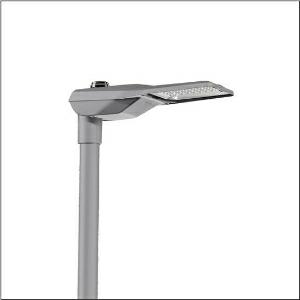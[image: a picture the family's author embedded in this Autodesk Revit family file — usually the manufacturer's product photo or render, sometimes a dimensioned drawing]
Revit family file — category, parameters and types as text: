
# Revit family: streetlight_sl_21_mini___p0_8a_5xe6u27n08hb_f017
name_source: partatom
category: Lighting Fixtures
units: mm (PartAtom-declared; Revit-internal decimal feet)

## family parameters
Cut with Voids When Loaded = No
Host = Face
Light Source = No
Part Type = Normal
Room Calculation Point = No
Round Connector Dimension = Use Diameter
Shared = No

## types (1)
- --- (1 x LED, 7550 lm, 66 W, 2200K)
    Apparent Load = 66 VA
    CIE Flux Codes = 33 69 96 100 100
    Color Rendering = 70
    Color Temperature = 2200K
    Default Elevation = 1800 mm
    Description = Streetlight SL 21 mini, mast luminaire, primary light control with lens, of PMMA, primary optical cover: cover, of toughened safety glass, transparent, light distribution: P0.8a, light emission: direct distribution, primary light characteristic: asymmetric, installation type: side-entry, LED, 3G 1.5mm², High Power LED, rated luminous flux: 7.550lm, luminous efficacy: 114lm/W, light colour: 722, colour temperature: 2200K, control gear: NEMA (7pin), control: flexible luminous flux parameterisation, time-dependent luminous flux control, constant luminous flux control, pre-setting: linear dimming characteristic, overheat protection, mains connection: 230..240V, AC, 50/60Hz, connection cable pre-assembled, cable length: 8,5m, wiring characteristics: H07RN-F, start of lifetime: 66W, end of service life: 69W, reduction: 30W, luminaire housing, of diecast aluminium (EN AC-44300), powder-coated, Siteco® metallic grey (DB 702S), corrosivity category C5 mid according to DIN EN ISO 12944, multi-level sealing system, sealing non-destructively replaceable, inclination adjustable: 0°, 5°, 10°, 15°, length: 628mm, width: 235mm, height: 110mm, spigot size: 42mm (side-entry), mounting height: 4..8m, protection rating (complete): IP66, insulation class (complete): insulation class I (protective earthing), certification: CE, ENEC, ENEC+, VDE, impact resistance: IK10, permissible operating ambient temperature for outdoor applications: -40..+50°C, standard-compliant lighting for roads and squares, packaging unit: 1 piece

Light Distribution: P0.8a
    Height = 110 mm
    Lamp = 1 x LED
    Lamp Light Flux = 7550 lm
    Lamp Power = 66 W
    Lamp count = 1
    Length = 625 mm
    Luminous efficacy = 114 lm/W
    Manufacturer = Siteco
    ModVariant = No
    Model = 5XE6U27N08HB
    Number of Poles = 1
    OnlyDefault = Yes
    Power Factor = 1
    Product Name = Streetlight SL 21 mini | P0.8a
    Product group = mast luminaire | pylon top
    ProductGroupID = 6100
    Protection Class = Protection class I
    Protection Degree = IP 66
    RLX_Detail_Level = 1
    RLX_Emergency_Light_Flux = 0 lm
    RLX_Emergency_Type = 0
    RLX_Emergency_Type_DB = No
    RlxData = <blob elided: 25897 chars, md5=512ba25e>
    Socket = socket
    Standby Power = 0 W
    System Light Flux = 7550 lm
    System Power = 66 W
    Type Comments = factory setting: luminous flux: 100 % | dim-lin: 254 | 670 mA
    Type Image = l_1294379.jpg
    URL = http://relux.com
    VarID = @adj_073582
    Voltage = 0 V
    Weight = 0.00 kg
    Width = 234 mm

## geometry (parser evidence)
native form markers: Blend x4, Sweep x12
no freeform markers — native parametric forms only
